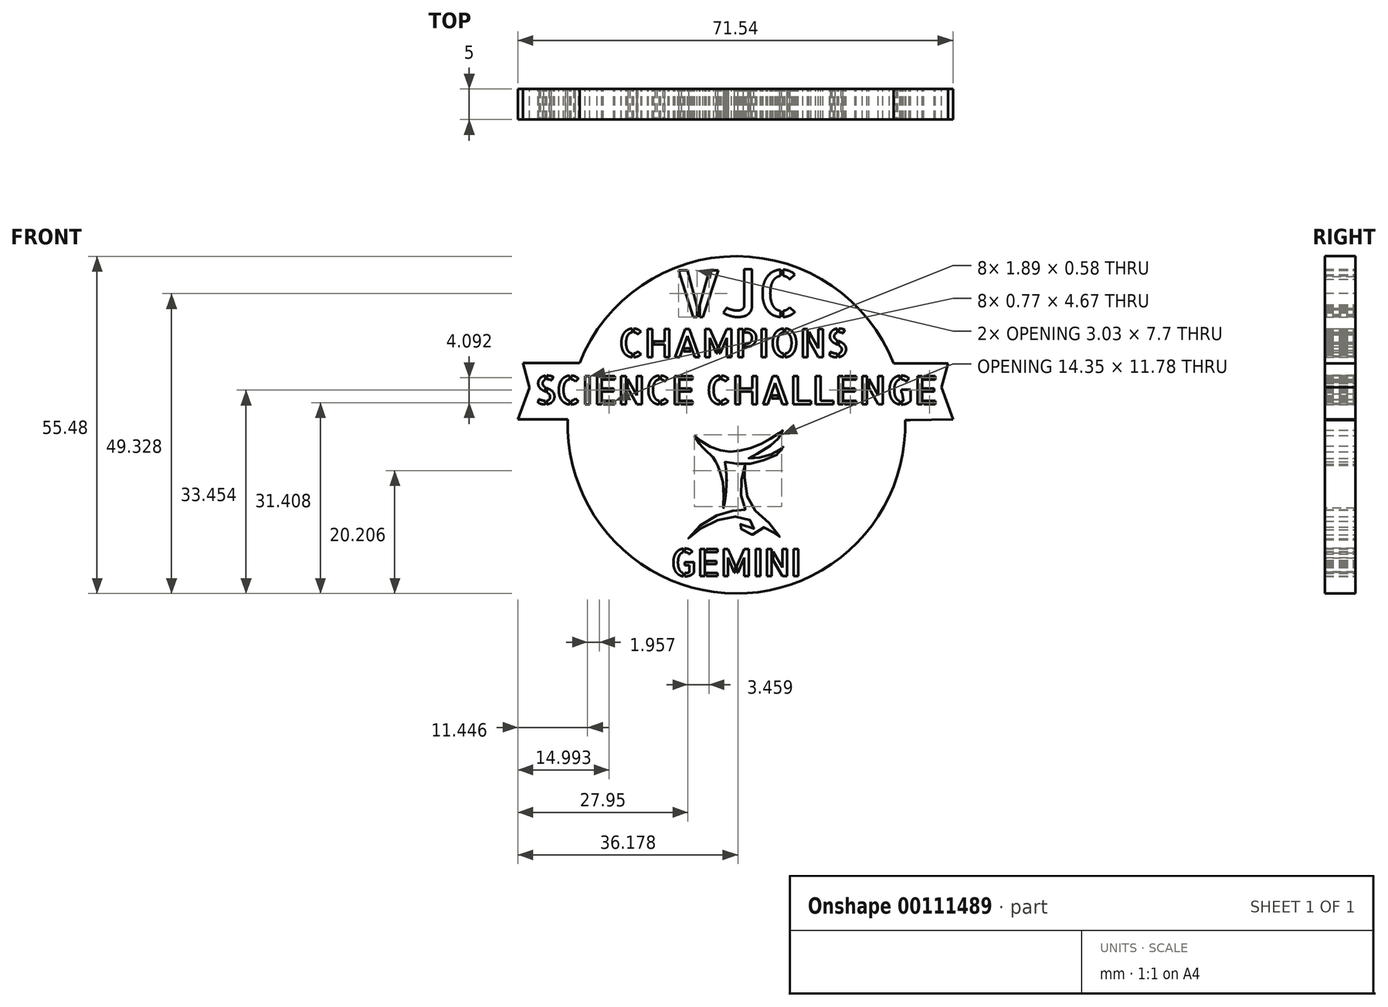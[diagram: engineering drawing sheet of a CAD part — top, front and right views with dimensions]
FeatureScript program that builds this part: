
annotation { "Feature Type Name" : "Feature", "Feature Type Description" : "" }
export const myFeature = defineFeature(function(context is Context, id is Id, definition is map)
    precondition{}
    {
        {
            var Q0;
            Q0=qCreatedBy(makeId("Front.planeOp"),FACE);
            var sketch = newSketch(context, id + "F0", { "sketchPlane" : qUnion([Q0])});
            skCircle(sketch, "E0", {"center": v(-0.65, -0.74) * mm, "radius": 27.74 * mm});
            skPoint(sketch, "E0.first.point", {"position": v(0, 27) * mm});
            skPoint(sketch, "E0.second.point", {"position": v(-1.07, -28.48) * mm});
            skPoint(sketch, "E0.third.point", {"position": v(-28.34, 0.92) * mm});
            skText(sketch, "E1", { "text": "CHAMPIONS", "fontName": "AllertaStencil-Regular.ttf"});
            skText(sketch, "E2", { "text": "GEMINI", "fontName": "AllertaStencil-Regular.ttf"});
            skLineSegment(sketch, "E3", {"start": v(-26.45, 9.45) * mm, "end": v(-35.78, 9.45) * mm});
            skLineSegment(sketch, "E4", {"start": v(-35.78, 9.45) * mm, "end": v(-34.66, 5.37) * mm});
            skLineSegment(sketch, "E5", {"start": v(-34.66, 5.37) * mm, "end": v(-36.58, 0.15) * mm});
            skLineSegment(sketch, "E6", {"start": v(-36.58, 0.15) * mm, "end": v(-28.38, 0.15) * mm});
            skLineSegment(sketch, "E7", {"start": v(25.2, 9.35) * mm, "end": v(34.13, 9.35) * mm});
            skLineSegment(sketch, "E8", {"start": v(34.13, 9.35) * mm, "end": v(33.08, 5.47) * mm});
            skLineSegment(sketch, "E9", {"start": v(33.08, 5.47) * mm, "end": v(34.96, 0.15) * mm});
            skLineSegment(sketch, "E10", {"start": v(34.96, 0.15) * mm, "end": v(27.09, 0) * mm});
            skFitSpline(sketch, "E11", {"points": [v(-7.58, -2.47) * mm, v(-6.81, -3.1) * mm, v(-5.48, -4.1) * mm, v(-4.07, -4.72) * mm, v(-2.43, -5.1) * mm, v(-1.24, -5.11) * mm, v(0.5, -4.9) * mm, v(2.28, -4.36) * mm, v(3.92, -3.59) * mm, v(5.25, -2.8) * mm, v(6.36, -2.09) * mm, v(6.6, -1.92) * mm, v(6.96, -1.63) * mm, v(6.55, -2.53) * mm, v(5.6, -3.57) * mm, v(3.6, -5.03) * mm, v(1.3, -6.2) * mm, v(2.4, -6.22) * mm, v(4.28, -5.87) * mm, v(6.18, -5) * mm, v(6.84, -4.5) * mm, v(7.02, -4.21) * mm, v(6.89, -4.9) * mm, v(4.88, -6.15) * mm, v(2.21, -7.02) * mm, v(-0.47, -7.17) * mm, v(-2.54, -6.8) * mm], "startDerivative": vector(22.31, -18.25) * mm, "endDerivative": vector(-43, 9.84) * mm});
            skFitSpline(sketch, "E12", {"points": [v(-7.58, -2.47) * mm, v(-6.77, -3.76) * mm, v(-5.4, -5.23) * mm, v(-4.6, -5.95) * mm, v(-3.85, -7.21) * mm, v(-3.12, -9.2) * mm, v(-2.76, -11.7) * mm, v(-2.79, -14.42) * mm, v(-2.53, -13.2) * mm, v(-2.27, -9.73) * mm, v(-2.5, -7.1) * mm, v(-2.54, -6.8) * mm], "startDerivative": vector(8.3, -15) * mm, "endDerivative": vector(-0.86, 6) * mm});
            skFitSpline(sketch, "E13", {"points": [v(0.75, -7.4) * mm, v(0.43, -8.37) * mm, v(0.09, -10.51) * mm, v(0.09, -12.04) * mm, v(0.48, -13.93) * mm, v(0.77, -14.7) * mm, v(0.24, -14.67) * mm, v(-1.6, -14.92) * mm, v(-3.24, -15.39) * mm, v(-5.56, -16.54) * mm, v(-7.6, -18.18) * mm, v(-8.54, -19.42) * mm, v(-7.5, -18.52) * mm, v(-5.25, -17.08) * mm, v(-2.87, -16.16) * mm, v(-0.75, -15.82) * mm, v(0.83, -16.04) * mm, v(2.13, -16.78) * mm, v(2.45, -17.43) * mm, v(1.87, -17.96) * mm, v(0.4, -17.56) * mm, v(-0.3, -16.62) * mm, v(-0.13, -17.55) * mm, v(0.77, -18.3) * mm, v(1.73, -18.77) * mm, v(3.25, -18.44) * mm, v(3.95, -17.55) * mm, v(4.8, -18.03) * mm, v(5.58, -18.58) * mm, v(6.56, -19.62) * mm, v(6.06, -18.43) * mm, v(4.7, -16.88) * mm, v(2.92, -15.28) * mm, v(1.75, -14.04) * mm, v(0.98, -11.93) * mm, v(0.66, -9.43) * mm, v(0.74, -8) * mm, v(0.75, -7.4) * mm]});
            skLineSegment(sketch, "E14", {"start": v(-26.45, 9.45) * mm, "end": v(26.52, 9.35) * mm});
            skLineSegment(sketch, "E15", {"start": v(-29.27, 0.15) * mm, "end": v(27.9, 0.02) * mm});
            skText(sketch, "E16", { "text": "SCIENCE CHALLENGE", "fontName": "AllertaStencil-Regular.ttf"});
            skText(sketch, "E17", { "text": "VJC", "fontName": "AllertaStencil-Regular.ttf"});
            const initialGuessF0  = {"E1": [-0.02007, 0.01041, 1, 0, 0.00464], "E2": [-0.0115, -0.02564, 1, 0, 0.0045], "E16": [-0.0338, 0.00264, 1, 0, 0.00467], "E17": [-0.01077, 0.01704, 1, 0, 0.00766]};
            skSetInitialGuess(sketch, initialGuessF0);
            skSolve(sketch);
        }
        {
            var Q0;
            Q0=makeQuery(id+"F0.imprint","IMPRINT",FACE,{"disambiguationData":[TD([[makeQuery(id+"F0.imprint","IMPRINT",EDGE,{"derivedFrom":sQuery(id+"F0.wireOp",EDGE,"E2.sketch_text.stroke-0")}),1.0]])]});
            var Q1;
            Q1=makeQuery(id+"F0.imprint","IMPRINT",FACE,{"disambiguationData":[TD([[makeQuery(id+"F0.imprint","IMPRINT",EDGE,{"derivedFrom":sQuery(id+"F0.wireOp",EDGE,"E1.sketch_text.stroke-0")}),1.0]])]});
            var Q2;
            {var subQ18=sQuery(id+"F0.wireOp",EDGE,"E8");Q2=makeQuery(id+"F0.imprint","IMPRINT",FACE,{"disambiguationData":[TD([[makeQuery(id+"F0.imprint","IMPRINT",EDGE,{"derivedFrom":subQ18}),-1.0]])]});}
            var Q3;
            {var subQ15=sQuery(id+"F0.wireOp",EDGE,"E16.sketch_text.stroke-54");Q3=makeQuery(id+"F0.imprint","IMPRINT",FACE,{"disambiguationData":[TD([[makeQuery(id+"F0.imprint","IMPRINT",EDGE,{"derivedFrom":subQ15}),1.0]])]});}
            var Q4;
            {var subQ13=sQuery(id+"F0.wireOp",EDGE,"E3");Q4=makeQuery(id+"F0.imprint","IMPRINT",FACE,{"disambiguationData":[TD([[makeQuery(id+"F0.imprint","IMPRINT",EDGE,{"derivedFrom":subQ13}),1.0]])]});}
            extrude(context, id + "F1", {"entities" : qUnion([Q0, Q1, Q2, Q3, Q4]), "depth" : 5 * mm});
        }
    });
